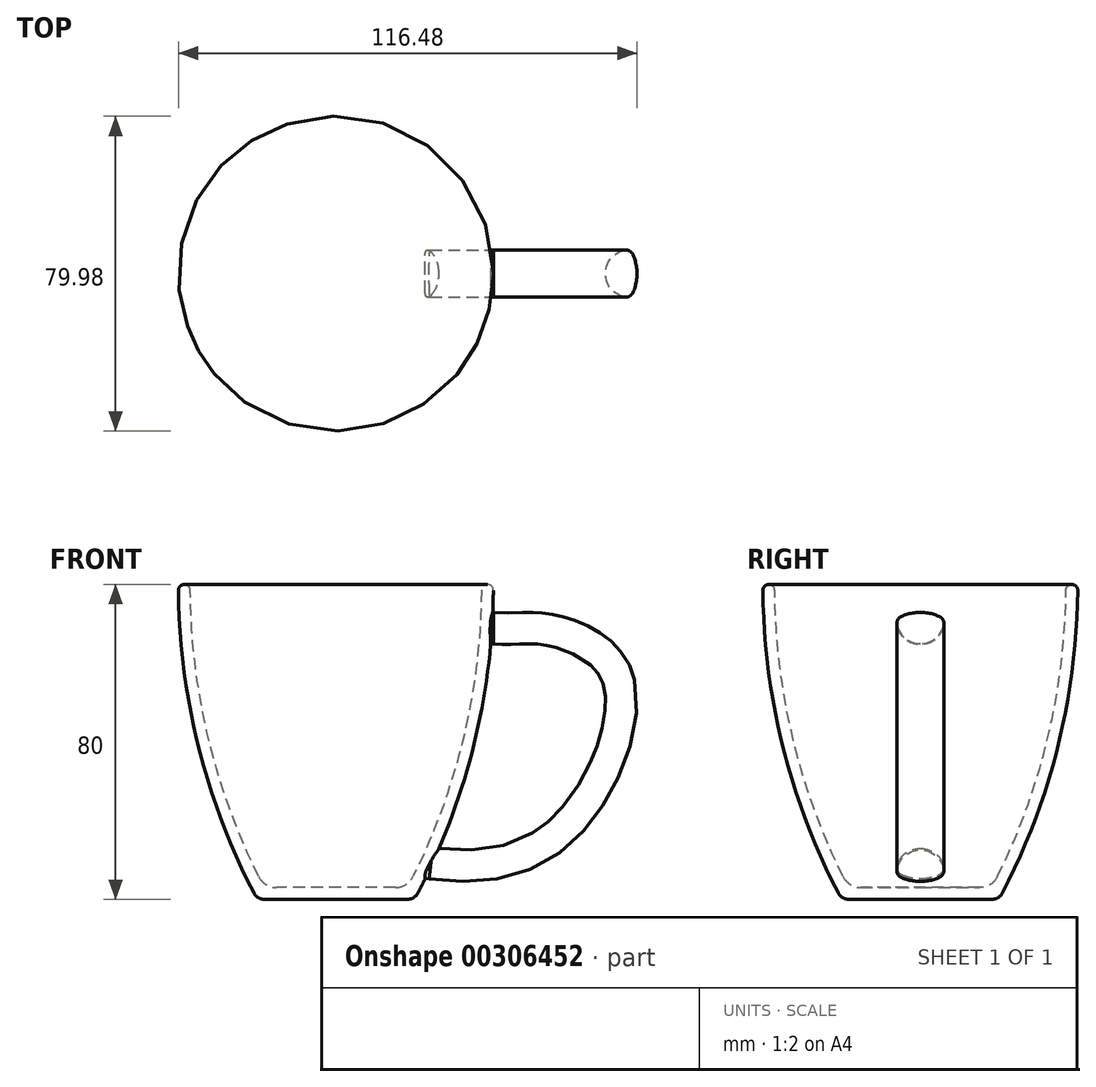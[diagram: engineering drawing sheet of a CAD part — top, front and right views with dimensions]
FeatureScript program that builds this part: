
annotation { "Feature Type Name" : "Feature", "Feature Type Description" : "" }
export const myFeature = defineFeature(function(context is Context, id is Id, definition is map)
    precondition{}
    {
        {
            var Q0;
            Q0=qCreatedBy(makeId("Front.planeOp"),FACE);
            var sketch = newSketch(context, id + "F0", { "sketchPlane" : qUnion([Q0])});
            skLineSegment(sketch, "E0", {"start": v(0, 3) * mm, "end": v(0, 0) * mm});
            skLineSegment(sketch, "E1", {"start": v(0, 0) * mm, "end": v(20, 0) * mm});
            skArc(sketch, "E2", {"start": v(20, 0) * mm, "mid": v(34.92, 38.77) * mm, "end": v(40, 80) * mm});
            skArc(sketch, "E3.0", {"start": v(18.19, 3) * mm, "mid": v(32.23, 40.37) * mm, "end": v(37, 80) * mm});
            skLineSegment(sketch, "E3.1", {"start": v(0, 3) * mm, "end": v(18.19, 3) * mm});
            skLineSegment(sketch, "E4", {"start": v(37, 80) * mm, "end": v(40, 80) * mm});
            skLineSegment(sketch, "E5", {"start": v(40, 160) * mm, "end": v(40, 0) * mm, "construction": true});
            skLineSegment(sketch, "E6", {"start": v(37, 160) * mm, "end": v(37, 0) * mm, "construction": true});
            skSolve(sketch);
        }
        {
            var Q0;
            Q0=qSketchRegion(id+"F0",true);
            var Q1;
            Q1=sQuery(id+"F0.wireOp",EDGE,"E0");
            revolve(context, id + "F1", {"entities" : qUnion([Q0]), "axis" : qUnion([Q1]), "revolveType" : RevolveType.FULL});
        }
        {
            var Q0;
            Q0=sQuery(id+"F0.wireOp",EDGE,"E5");
            cPlane(context, id + "F2", {"entities" : qUnion([Q0]), "cplaneType" : CPlaneType.LINE_ANGLE, "offset" : 150 * mm, "angle" : 0 * degree, "width" : 150 * mm, "height" : 150 * mm});
        }
        {
            var Q0;
            Q0=qCreatedBy(id+"F2.planeOp",FACE);
            var sketch = newSketch(context, id + "F3", { "sketchPlane" : qUnion([Q0])});
            skPoint(sketch, "E7", {"position": v(0, 70) * mm});
            skArc(sketch, "E8", {"start": v(4.8, 71.83) * mm, "mid": v(0, 72.83) * mm, "end": v(-4.8, 71.83) * mm});
            skArc(sketch, "E9", {"start": v(4.8, 71.83) * mm, "mid": v(5.79, 70.9) * mm, "end": v(5.95, 69.54) * mm});
            skArc(sketch, "E10", {"start": v(-4.8, 71.83) * mm, "mid": v(-5.79, 70.9) * mm, "end": v(-5.95, 69.54) * mm});
            skArc(sketch, "E11", {"start": v(-5.95, 69.54) * mm, "mid": v(0, 64.83) * mm, "end": v(5.95, 69.54) * mm});
            skSolve(sketch);
        }
        {
            var Q0;
            Q0=qSketchRegion(id+"F3",true);
            extrude(context, id + "F4", {"entities" : qUnion([Q0]), "operationType" : NewBodyOperationType.ADD, "endBound" : BoundingType.UP_TO_NEXT, "depth" : 25 * mm});
        }
        {
            var Q0;
            Q0=qCreatedBy(makeId("Front.planeOp"),FACE);
            var sketch = newSketch(context, id + "F5", { "sketchPlane" : qUnion([Q0])});
            skLineSegment(sketch, "E12", {"start": v(42.52, 70) * mm, "end": v(37.48, 70) * mm, "construction": true});
            skFitSpline(sketch, "E13", {"points": [v(40, 70) * mm, v(54.73, 69.58) * mm, v(72.29, 57.65) * mm, v(60.98, 19.5) * mm, v(24, 8) * mm], "startDerivative": vector(122.83, -3.58) * mm, "endDerivative": vector(-160.62, 21.78) * mm});
            skSolve(sketch);
        }
        {
            var Q0;
            Q0=makeQuery(id+"F3.imprint","IMPRINT",FACE,{"disambiguationData":[TD([[makeQuery(id+"F3.imprint","IMPRINT",EDGE,{"derivedFrom":sQuery(id+"F3.wireOp",EDGE,"E8")}),1.0]])]});
            var Q1;
            Q1=sQuery(id+"F5.wireOp",EDGE,"E13");
            sweep(context, id + "F6", {"operationType" : NewBodyOperationType.ADD, "profiles" : qUnion([Q0]), "path" : qUnion([Q1])});
        }
        {
            var Q0;
            Q0=makeQuery(id+"F1.opRevolve","SWEPT_EDGE",EDGE,{"disambiguationData":[OSD([sQuery(id+"F0.wireOp",EDGE,"E3.0"),sQuery(id+"F0.wireOp",EDGE,"E4")])]});
            var Q1;
            Q1=makeQuery(id+"F1.opRevolve","SWEPT_EDGE",EDGE,{"disambiguationData":[OSD([sQuery(id+"F0.wireOp",EDGE,"E2"),sQuery(id+"F0.wireOp",EDGE,"E4")])]});
            fillet(context, id + "F7", {"entities" : qUnion([Q0, Q1]), "radius" : 1.5 * mm, "tangentPropagation" : true, "allowEdgeOverflow" : false});
        }
        {
            var Q0;
            Q0=makeQuery(id+"F1.opRevolve","SWEPT_EDGE",EDGE,{"disambiguationData":[OSD([sQuery(id+"F0.wireOp",EDGE,"E1"),sQuery(id+"F0.wireOp",EDGE,"E2")])]});
            fillet(context, id + "F8", {"entities" : qUnion([Q0]), "radius" : 3 * mm, "tangentPropagation" : true, "allowEdgeOverflow" : false});
        }
        {
            var Q0;
            Q0=makeQuery(id+"F1.opRevolve","SWEPT_EDGE",EDGE,{"disambiguationData":[OSD([sQuery(id+"F0.wireOp",EDGE,"E3.0"),sQuery(id+"F0.wireOp",EDGE,"E3.1")])]});
            fillet(context, id + "F9", {"entities" : qUnion([Q0]), "radius" : 5 * mm, "tangentPropagation" : true, "allowEdgeOverflow" : false});
        }
        {
            var Q0;
            Q0=makeQuery(id+"F6.opSweep","CAP_FACE",FACE,{"disambiguationData":[OSD([sQuery(id+"F3.wireOp",EDGE,"E8"),sQuery(id+"F3.wireOp",EDGE,"E9"),sQuery(id+"F3.wireOp",EDGE,"E10"),sQuery(id+"F3.wireOp",EDGE,"E11"),sQuery(id+"F5.wireOp",VERTEX,"b8e06edf-8505-42d8-96b9-aa2b29730343.end")])],"isStart":false});
            var sketch = newSketch(context, id + "F10", { "sketchPlane" : qUnion([Q0])});
            skArc(sketch, "E14", {"start": v(5.95, 10.95) * mm, "mid": v(5.75, 11.6) * mm, "end": v(5.49, 12.23) * mm});
            skArc(sketch, "E15", {"start": v(4.8, 8.65) * mm, "mid": v(5.79, 9.6) * mm, "end": v(5.95, 10.95) * mm});
            skArc(sketch, "E16", {"start": v(-4.8, 8.65) * mm, "mid": v(0, 7.65) * mm, "end": v(4.8, 8.65) * mm});
            skArc(sketch, "E17", {"start": v(-5.95, 10.95) * mm, "mid": v(-5.79, 9.6) * mm, "end": v(-4.8, 8.65) * mm});
            skArc(sketch, "E18", {"start": v(-5.49, 12.23) * mm, "mid": v(-5.75, 11.6) * mm, "end": v(-5.95, 10.95) * mm});
            skLineSegment(sketch, "E19", {"start": v(5.49, 12.23) * mm, "end": v(-5.49, 12.23) * mm});
            skSolve(sketch);
        }
        {
            var Q0;
            Q0=qSketchRegion(id+"F10",true);
            var Q1;
            Q1=makeQuery(id+"F1.opRevolve","SWEPT_FACE",FACE,{"disambiguationData":[OSD([sQuery(id+"F0.wireOp",EDGE,"E3.0")])]});
            extrude(context, id + "F11", {"entities" : qUnion([Q0]), "operationType" : NewBodyOperationType.ADD, "endBound" : BoundingType.UP_TO_SURFACE, "endBoundEntityFace" : qUnion([Q1]), "depth" : 25 * mm});
        }
    });
